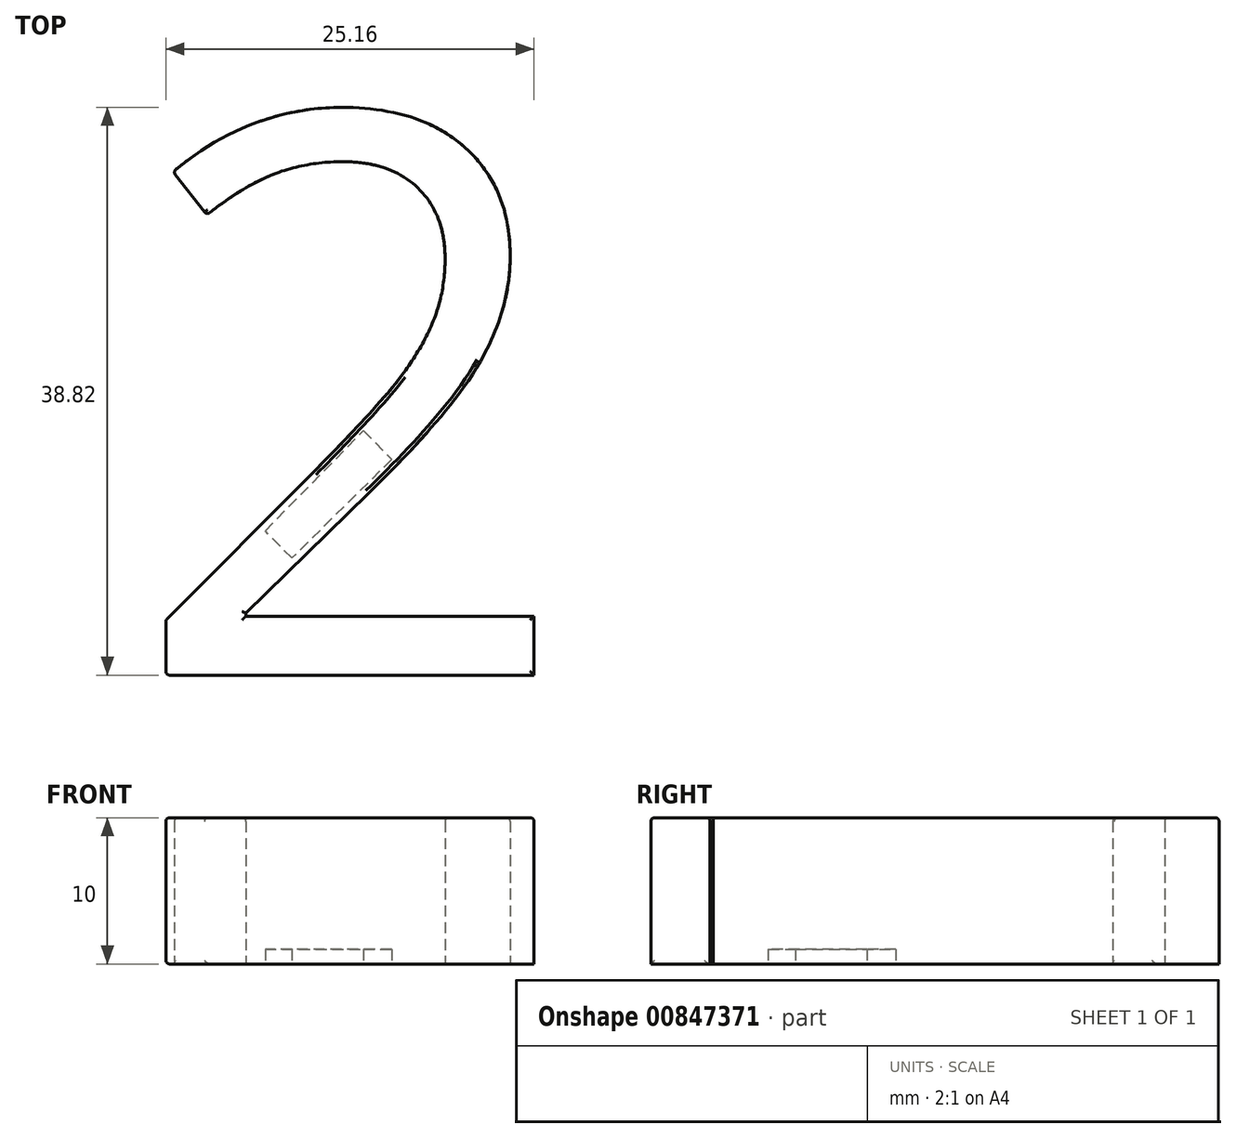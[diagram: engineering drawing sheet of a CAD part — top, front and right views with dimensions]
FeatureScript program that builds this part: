
annotation { "Feature Type Name" : "Feature", "Feature Type Description" : "" }
export const myFeature = defineFeature(function(context is Context, id is Id, definition is map)
    precondition{}
    {
        {
            var Q0;
            Q0=qCreatedBy(makeId("Top.planeOp"),FACE);
            var sketch = newSketch(context, id + "F0", { "sketchPlane" : qUnion([Q0])});
            skText(sketch, "E0", { "text": "2", "fontName": "OpenSans-Regular.ttf"});
            const initialGuessF0  = {"E0": [-0.02189, -0.01908, 1, 0, 0.0386]};
            skSetInitialGuess(sketch, initialGuessF0);
            skSolve(sketch);
        }
        {
            var Q0;
            Q0 = qSketchRegion(id + "F0", true);
            extrude(context, id + "F1", {"entities" : qUnion([Q0]), "depth" : 10 * mm, "offsetDistance" : 25 * mm});
        }
        {
            var Q0;
            Q0=makeQuery(id+"F1.opExtrude","CAP_FACE",FACE,{"disambiguationData":[OSD([sQuery(id+"F0.wireOp",EDGE,"E0.sketch_text.stroke-0"),sQuery(id+"F0.wireOp",EDGE,"E0.sketch_text.stroke-1"),sQuery(id+"F0.wireOp",EDGE,"E0.sketch_text.stroke-2"),sQuery(id+"F0.wireOp",EDGE,"E0.sketch_text.stroke-3"),sQuery(id+"F0.wireOp",EDGE,"E0.sketch_text.stroke-4"),sQuery(id+"F0.wireOp",EDGE,"E0.sketch_text.stroke-5"),sQuery(id+"F0.wireOp",EDGE,"E0.sketch_text.stroke-6"),sQuery(id+"F0.wireOp",EDGE,"E0.sketch_text.stroke-7"),sQuery(id+"F0.wireOp",EDGE,"E0.sketch_text.stroke-8"),sQuery(id+"F0.wireOp",EDGE,"E0.sketch_text.stroke-9"),sQuery(id+"F0.wireOp",EDGE,"E0.sketch_text.stroke-10"),sQuery(id+"F0.wireOp",EDGE,"E0.sketch_text.stroke-11"),sQuery(id+"F0.wireOp",EDGE,"E0.sketch_text.stroke-12"),sQuery(id+"F0.wireOp",EDGE,"E0.sketch_text.stroke-13"),sQuery(id+"F0.wireOp",EDGE,"E0.sketch_text.stroke-14"),sQuery(id+"F0.wireOp",EDGE,"E0.sketch_text.stroke-15"),sQuery(id+"F0.wireOp",EDGE,"E0.sketch_text.stroke-16"),sQuery(id+"F0.wireOp",EDGE,"E0.sketch_text.stroke-17"),sQuery(id+"F0.wireOp",EDGE,"E0.sketch_text.stroke-18"),sQuery(id+"F0.wireOp",EDGE,"E0.sketch_text.stroke-19")])],"isStart":true});
            var sketch = newSketch(context, id + "F2", { "sketchPlane" : qUnion([Q0])});
            skLineSegment(sketch, "E1", {"start": v(-13.18, 9.23) * mm, "end": v(-5.77, 1.65) * mm});
            skLineSegment(sketch, "E2", {"start": v(-5.77, 1.65) * mm, "end": v(-3.12, 4.33) * mm});
            skLineSegment(sketch, "E3", {"start": v(-3.12, 4.33) * mm, "end": v(-10.66, 11.78) * mm});
            skLineSegment(sketch, "E4", {"start": v(-10.66, 11.78) * mm, "end": v(-13.18, 9.23) * mm});
            skLineSegment(sketch, "E5.0", {"start": v(-10.66, 11.07) * mm, "end": v(-12.48, 9.22) * mm});
            skLineSegment(sketch, "E5.1", {"start": v(-3.82, 4.33) * mm, "end": v(-10.66, 11.07) * mm});
            skLineSegment(sketch, "E5.2", {"start": v(-5.76, 2.36) * mm, "end": v(-3.82, 4.33) * mm});
            skLineSegment(sketch, "E5.3", {"start": v(-12.48, 9.22) * mm, "end": v(-5.76, 2.36) * mm});
            skSolve(sketch);
        }
        {
            var Q0;
            Q0=makeQuery(id+"F2.imprint","IMPRINT",FACE,{"disambiguationData":[TD([[makeQuery(id+"F2.imprint","IMPRINT",EDGE,{"derivedFrom":sQuery(id+"F2.wireOp",EDGE,"E5.0")}),1.0]])]});
            extrude(context, id + "F3", {"entities" : qUnion([Q0]), "operationType" : NewBodyOperationType.REMOVE, "oppositeDirection" : true, "depth" : 1 * mm, "offsetDistance" : 25 * mm});
        }
        {
            var Q0;
            Q0=makeQuery(id+"F1.opExtrude","CAP_FACE",FACE,{"disambiguationData":[OSD([sQuery(id+"F0.wireOp",EDGE,"E0.sketch_text.stroke-0"),sQuery(id+"F0.wireOp",EDGE,"E0.sketch_text.stroke-1"),sQuery(id+"F0.wireOp",EDGE,"E0.sketch_text.stroke-2"),sQuery(id+"F0.wireOp",EDGE,"E0.sketch_text.stroke-3"),sQuery(id+"F0.wireOp",EDGE,"E0.sketch_text.stroke-4"),sQuery(id+"F0.wireOp",EDGE,"E0.sketch_text.stroke-5"),sQuery(id+"F0.wireOp",EDGE,"E0.sketch_text.stroke-6"),sQuery(id+"F0.wireOp",EDGE,"E0.sketch_text.stroke-7"),sQuery(id+"F0.wireOp",EDGE,"E0.sketch_text.stroke-8"),sQuery(id+"F0.wireOp",EDGE,"E0.sketch_text.stroke-9"),sQuery(id+"F0.wireOp",EDGE,"E0.sketch_text.stroke-10"),sQuery(id+"F0.wireOp",EDGE,"E0.sketch_text.stroke-11"),sQuery(id+"F0.wireOp",EDGE,"E0.sketch_text.stroke-12"),sQuery(id+"F0.wireOp",EDGE,"E0.sketch_text.stroke-13"),sQuery(id+"F0.wireOp",EDGE,"E0.sketch_text.stroke-14"),sQuery(id+"F0.wireOp",EDGE,"E0.sketch_text.stroke-15"),sQuery(id+"F0.wireOp",EDGE,"E0.sketch_text.stroke-16"),sQuery(id+"F0.wireOp",EDGE,"E0.sketch_text.stroke-17"),sQuery(id+"F0.wireOp",EDGE,"E0.sketch_text.stroke-18"),sQuery(id+"F0.wireOp",EDGE,"E0.sketch_text.stroke-19")])],"isStart":false});
            var Q1;
            Q1=makeQuery(id+"F1.opExtrude","SWEPT_FACE",FACE,{"disambiguationData":[OSD([sQuery(id+"F0.wireOp",EDGE,"E0.sketch_text.stroke-1")])]});
            var Q2;
            Q2=makeQuery(id+"F1.opExtrude","SWEPT_FACE",FACE,{"disambiguationData":[OSD([sQuery(id+"F0.wireOp",EDGE,"E0.sketch_text.stroke-10")])]});
            fillet(context, id + "F4", {"entities" : qUnion([Q0, Q1, Q2]), "radius" : .25 * mm, "tangentPropagation" : true, "allowEdgeOverflow" : false});
        }
    });
